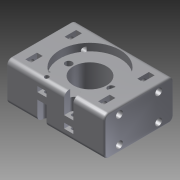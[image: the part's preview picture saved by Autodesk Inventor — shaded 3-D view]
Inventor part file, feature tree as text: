
AUTODESK INVENTOR PART (.ipt)
format: ipt  version: 2012 (Build 160160000, 160)  size: 372,736 bytes
history: native  units: mm
features: extrude x13, sketch x13, fillet x3, chamfer x1
ambient origin geometry x8: Origin, YZ Plane, XZ Plane, XY Plane, X Axis, Y Axis, Z Axis, Center Point
bodies: Solid1 (feature_tree)
feature tree (30):
  extrude  "Extrusion1"  Depth=60.0mm
  extrude  "Extrusion2"  Depth=21.2mm
  extrude  "Extrusion3"  Depth=24.0mm TaperAngle=0.0deg
  fillet  "Fillet1"  Radius=4.2mm
  fillet  "Fillet2"  Radius=9.2mm
  extrude  "Extrusion4"  Depth=9.2mm
  extrude  "Extrusion5"  Depth=4.0mm
  extrude  "Extrusion6"  Depth=4.0mm
  extrude  "Extrusion7"  Depth=16.0mm TaperAngle=0.0deg
  extrude  "Extrusion8"  Depth=4.0mm
  extrude  "Extrusion9"  Depth=4.0mm
  extrude  "Extrusion10"  Depth=9.2mm
  fillet  "Fillet3"  Radius=9.2mm
  chamfer  "Chamfer1"  Distance=16.0mm
  extrude  "Extrusion11"  Depth=1.0mm
  extrude  "Extrusion12"  Depth=3.5mm
  extrude  "Extrusion13"  Depth=6.0mm
  sketch  "Sketch1"  dims[d0=42.4mm d1=60.0mm]
  sketch  "Sketch2"  dims[d2=20.3mm d3=21.2mm]
  sketch  "Sketch3"  dims[d4=30.0mm d5=24.0mm d6=0.0mm d7=4.2mm d8=9.2mm]
  sketch  "Sketch4"  dims[d9=9.2mm d10=9.2mm]
  sketch  "Sketch5"  dims[d11=9.2mm d12=4.0mm]
  sketch  "Sketch6"  dims[d13=4.0mm d14=4.0mm]
  sketch  "Sketch7"  dims[d15=4.0mm d16=16.0mm d17=0.0mm]
  sketch  "Sketch8"  dims[d18=4.2mm d19=4.0mm]
  sketch  "Sketch10"  dims[d20=4.0mm d21=4.0mm]
  sketch  "Sketch11"  dims[d22=4.0mm d23=9.2mm d24=9.2mm]
  sketch  "Sketch12"  dims[d25=9.2mm]
  sketch  "Sketch13"  dims[d26=9.2mm d27=16.0mm d28=0.0mm]
  sketch  "Sketch14"  dims[d29=3.0mm d30=1.0mm d31=3.5mm d32=6.0mm d33=5.65mm d34=7.1mm d35=5.65mm d36=6.0mm d37=18.0mm d38=0.0mm d39=36.8mm d40=4.5mm d41=0.0mm d42=4.2mm d43=21.2mm d44=21.2mm d45=26.0mm d46=17.0mm d47=4.5mm d48=0.0mm d49=7.1mm d50=5.0mm d51=0.0mm d52=0.2mm d53=0.0mm d54=5.6mm d56=12.0mm d57=19.0mm d58=19.0mm d59=3.2mm d60=4.0mm d61=4.0mm d62=6.0mm d63=0.0mm d64=2.5mm d65=3.0mm d66=3.0mm d67=2.8mm d68=2.8mm d69=7.0mm d70=0.0mm d71=2.8mm d72=1.5mm d73=2.0mm d74=45.0deg d75=0.2mm d76=0.0mm d77=0.2mm d78=0.0mm d79=0.2mm d80=0.0mm]
